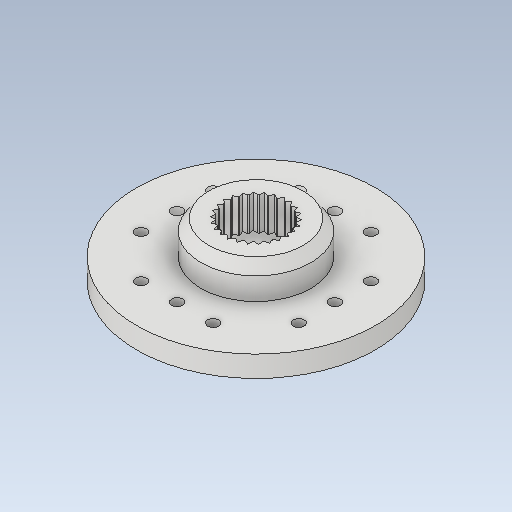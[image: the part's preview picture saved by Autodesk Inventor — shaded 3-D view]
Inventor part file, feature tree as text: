
AUTODESK INVENTOR PART (.ipt)
format: ipt  version: 2020 (Build 240168000, 168)  size: 295,424 bytes
history: native  units: mm
features: extrude x7, sketch x7, other x1, chamfer x1, pattern_circular x1
ambient origin geometry x8: Origin, YZ Plane, XZ Plane, XY Plane, X Axis, Y Axis, Z Axis, Center Point
bodies: Body1 (feature_tree)
feature tree (17):
  other  "Sólido1"
  extrude  "Extrusión1"  Depth=1.0mm
  extrude  "Extrusión2"  Depth=7.1mm
  chamfer  "Chaflán1"  Distance=40.0mm Angle=360.0deg
  extrude  "Extrusión4"  Depth=1.9mm
  extrude  "Extrusión5"  Depth=3.0mm
  extrude  "Extrusión7"  Depth=0.5mm
  pattern_circular  "Patrón circular1"  [2 undecoded]
  extrude  "Extrusión8"  Depth=3.0mm
  extrude  "Extrusión9"  Depth=3.0mm
  sketch  "Boceto1"  dims[d0=21.5mm d1=1.0mm]
  sketch  "Boceto2"  dims[d2=6.5mm d4=7.1mm d5=40.0mm d7=360.0deg]
  sketch  "Boceto6"  dims[d9=1.9mm d10=0.0mm d11=9.9mm]
  sketch  "Boceto7"  dims[d12=3.0mm d13=0.0mm d18=0.7mm d19=2.0mm d20=9.599311mm]
  sketch  "Boceto9"  dims[d24=6.5mm d25=0.5mm]
  sketch  "Boceto10"  dims[d26=1.0mm d27=0.0mm]
  sketch  "Boceto11"  dims[d28=8.5mm d29=0.4mm d30=0.0mm d34=5.2mm d37=13.962634mm d38=0.525825mm d39=3.0mm d40=0.0mm d41=260.0mm d42=360.0deg d44=3.0mm d45=0.0mm d46=2.8mm d47=3.0mm d48=0.0mm]
note: 2 required parameter values undecoded (feature->parameter linkage not recoverable at this tier; creation-order binding heuristic only, values carry confidence <= 0.55)
